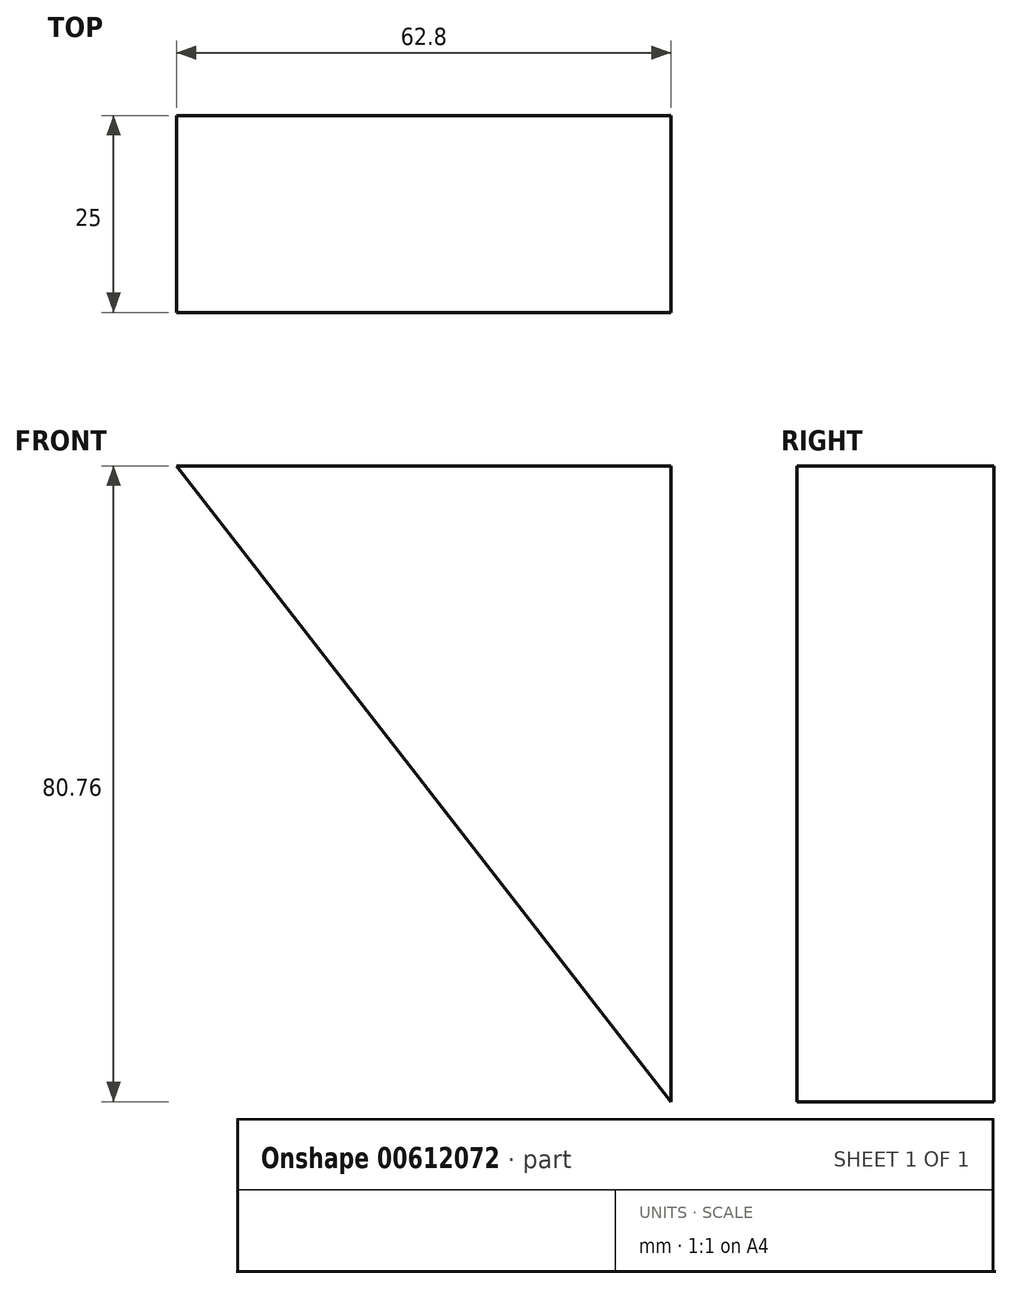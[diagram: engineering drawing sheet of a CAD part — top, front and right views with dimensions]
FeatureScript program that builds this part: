
annotation { "Feature Type Name" : "Feature", "Feature Type Description" : "" }
export const myFeature = defineFeature(function(context is Context, id is Id, definition is map)
    precondition{}
    {
        {
            var Q0;
            Q0=qCreatedBy(makeId("Front.planeOp"),FACE);
            var sketch = newSketch(context, id + "F0", { "sketchPlane" : qUnion([Q0])});
            skLineSegment(sketch, "E0.bottom", {"start": v(-31.4, 40.38) * mm, "end": v(31.4, 40.38) * mm});
            skLineSegment(sketch, "E0.top", {"start": v(-31.4, -40.38) * mm, "end": v(31.4, -40.38) * mm});
            skLineSegment(sketch, "E0.left", {"start": v(-31.4, 40.38) * mm, "end": v(-31.4, -40.38) * mm});
            skLineSegment(sketch, "E0.right", {"start": v(31.4, 40.38) * mm, "end": v(31.4, -40.38) * mm});
            skPoint(sketch, "E0.middle", {"position": v(0, 0) * mm});
            skLineSegment(sketch, "E1", {"start": v(-31.4, 40.38) * mm, "end": v(31.4, -40.38) * mm});
            skSolve(sketch);
        }
        {
            var Q0;
            Q0=makeQuery(id+"F0.imprint","IMPRINT",FACE,{"disambiguationData":[TD([[makeQuery(id+"F0.imprint","IMPRINT",EDGE,{"derivedFrom":sQuery(id+"F0.wireOp",EDGE,"E0.bottom")}),-1.0]])]});
            extrude(context, id + "F1", {"entities" : qUnion([Q0]), "depth" : 25 * mm, "offsetDistance" : 25 * mm});
        }
    });
